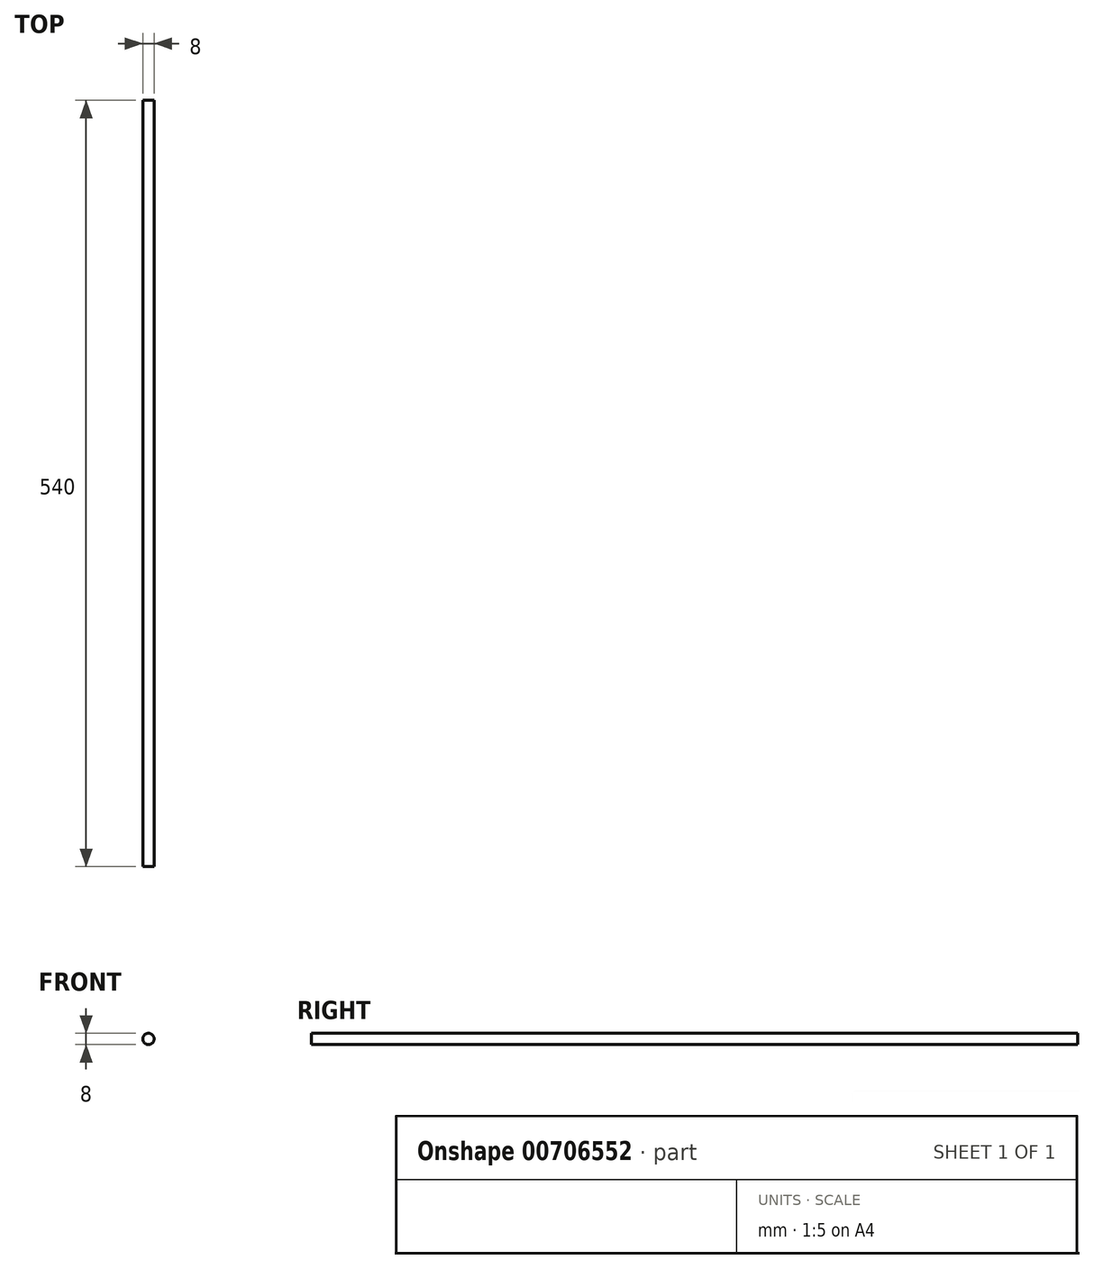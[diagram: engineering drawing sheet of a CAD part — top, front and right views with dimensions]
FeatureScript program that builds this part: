
annotation { "Feature Type Name" : "Feature", "Feature Type Description" : "" }
export const myFeature = defineFeature(function(context is Context, id is Id, definition is map)
    precondition{}
    {
        {
            var Q0;
            Q0=qCreatedBy(makeId("Front.planeOp"),FACE);
            var sketch = newSketch(context, id + "F0", { "sketchPlane" : qUnion([Q0])});
            skCircle(sketch, "E0", {"center": v(0, 0) * mm, "radius": 4 * mm});
            skSolve(sketch);
        }
        {
            var Q0;
            Q0 = qSketchRegion(id + "F0", true);
            extrude(context, id + "F1", {"entities" : qUnion([Q0]), "depth" : 540 * mm, "offsetDistance" : 25.4 * mm});
        }
    });
